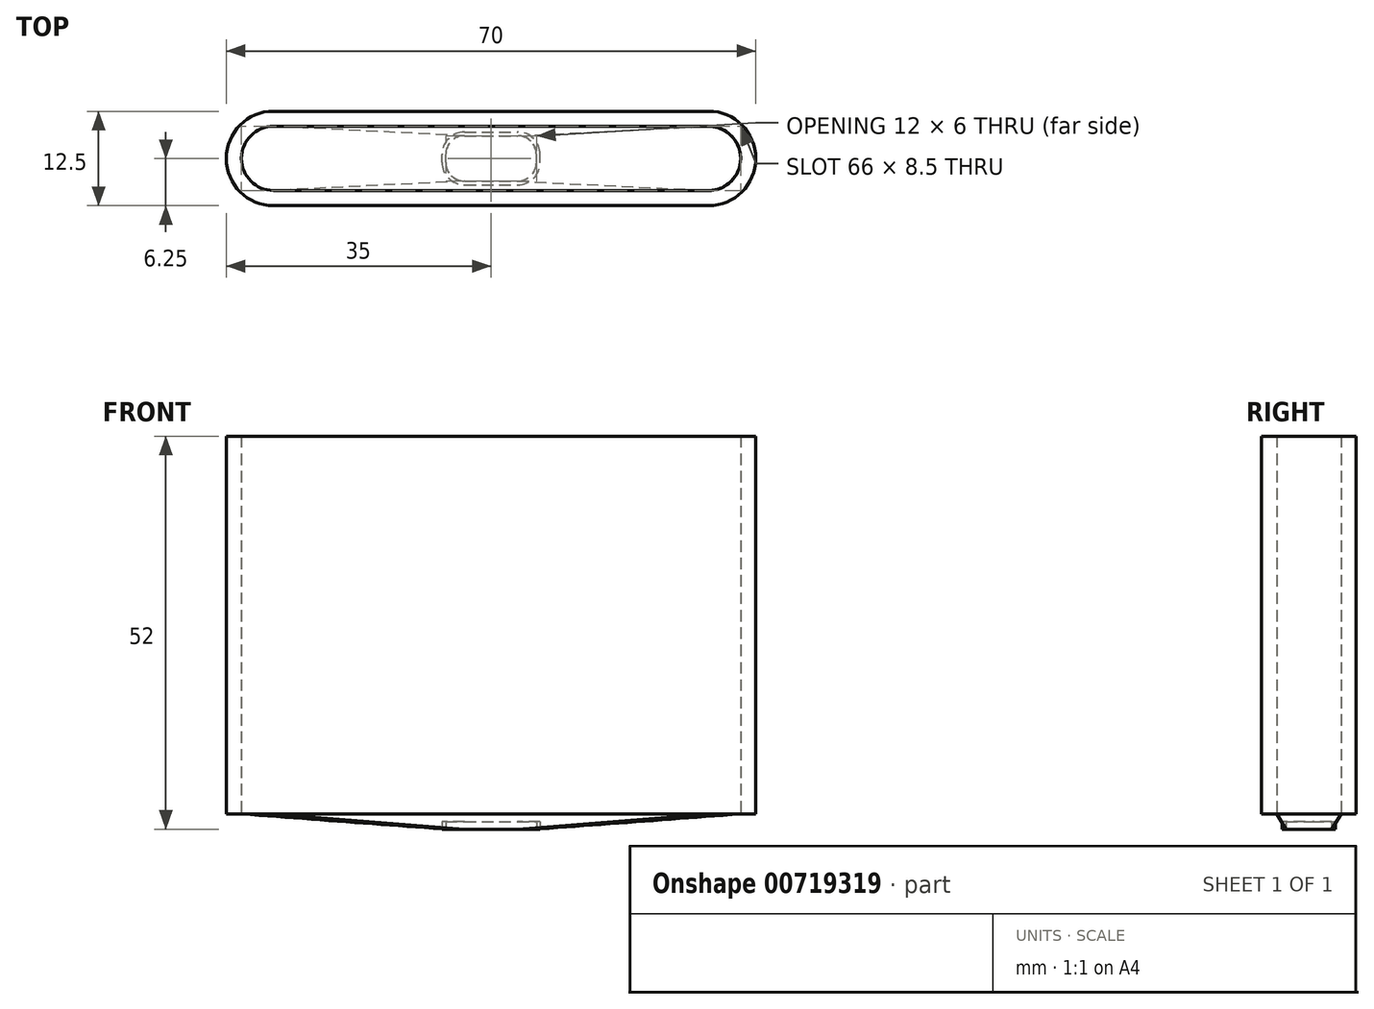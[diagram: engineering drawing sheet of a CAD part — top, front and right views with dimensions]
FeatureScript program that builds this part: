
annotation { "Feature Type Name" : "Feature", "Feature Type Description" : "" }
export const myFeature = defineFeature(function(context is Context, id is Id, definition is map)
    precondition{}
    {
        {
            var Q0;
            Q0=qCreatedBy(makeId("Top.planeOp"),FACE);
            var sketch = newSketch(context, id + "F0", { "sketchPlane" : qUnion([Q0])});
            skLineSegment(sketch, "E0.bottom", {"start": v(28.75, 6.25) * mm, "end": v(-28.75, 6.25) * mm});
            skLineSegment(sketch, "E0.top", {"start": v(28.75, -6.25) * mm, "end": v(-28.75, -6.25) * mm});
            skLineSegment(sketch, "E0.left", {"start": v(35, 0) * mm, "end": v(35, 0) * mm});
            skLineSegment(sketch, "E0.right", {"start": v(-35, 0) * mm, "end": v(-35, 0) * mm});
            skPoint(sketch, "E0.middle", {"position": v(0, 0) * mm});
            skLineSegment(sketch, "E1.bottom", {"start": v(-3.5, -3) * mm, "end": v(3.5, -3) * mm});
            skLineSegment(sketch, "E1.top", {"start": v(-3.5, 3) * mm, "end": v(3.5, 3) * mm});
            skLineSegment(sketch, "E1.left", {"start": v(-6, -0.5) * mm, "end": v(-6, 0.5) * mm});
            skLineSegment(sketch, "E1.right", {"start": v(6, -0.5) * mm, "end": v(6, 0.5) * mm});
            skLineSegment(sketch, "E2", {"start": v(0, -37.66) * mm, "end": v(0, 28.64) * mm, "construction": true});
            skLineSegment(sketch, "E3.bottom", {"start": v(13, 3) * mm, "end": v(26, 3) * mm});
            skLineSegment(sketch, "E3.top", {"start": v(13, -3) * mm, "end": v(26, -3) * mm});
            skLineSegment(sketch, "E3.left", {"start": v(10.5, 0.5) * mm, "end": v(10.5, -0.5) * mm});
            skLineSegment(sketch, "E3.right", {"start": v(28.5, 0.5) * mm, "end": v(28.5, -0.5) * mm});
            skPoint(sketch, "E4.visualSharp", {"position": v(-6, -3) * mm});
            skArc(sketch, "E4.filletArc", {"start": v(-6, -0.5) * mm, "mid": v(-5.27, -2.27) * mm, "end": v(-3.5, -3) * mm});
            skPoint(sketch, "E5.visualSharp", {"position": v(6, 3) * mm});
            skArc(sketch, "E5.filletArc", {"start": v(6, 0.5) * mm, "mid": v(5.27, 2.27) * mm, "end": v(3.5, 3) * mm});
            skPoint(sketch, "E6.visualSharp", {"position": v(6, -3) * mm});
            skArc(sketch, "E6.filletArc", {"start": v(3.5, -3) * mm, "mid": v(5.27, -2.27) * mm, "end": v(6, -0.5) * mm});
            skPoint(sketch, "E7.visualSharp", {"position": v(-6, 3) * mm});
            skArc(sketch, "E7.filletArc", {"start": v(-3.5, 3) * mm, "mid": v(-5.27, 2.27) * mm, "end": v(-6, 0.5) * mm});
            skLineSegment(sketch, "E8.MirrorCS", {"start": v(-13, 3) * mm, "end": v(-26, 3) * mm});
            skLineSegment(sketch, "E9.MirrorCS", {"start": v(-10.5, 0.5) * mm, "end": v(-10.5, -0.5) * mm});
            skLineSegment(sketch, "E10.MirrorCS", {"start": v(-13, -3) * mm, "end": v(-26, -3) * mm});
            skLineSegment(sketch, "E11.MirrorCS", {"start": v(-28.5, 0.5) * mm, "end": v(-28.5, -0.5) * mm});
            skPoint(sketch, "E12.visualSharp", {"position": v(10.5, -3) * mm});
            skArc(sketch, "E12.filletArc", {"start": v(10.5, -0.5) * mm, "mid": v(11.23, -2.27) * mm, "end": v(13, -3) * mm});
            skPoint(sketch, "E13.visualSharp", {"position": v(10.5, 3) * mm});
            skArc(sketch, "E13.filletArc", {"start": v(13, 3) * mm, "mid": v(11.23, 2.27) * mm, "end": v(10.5, 0.5) * mm});
            skPoint(sketch, "E14.visualSharp", {"position": v(28.5, 3) * mm});
            skArc(sketch, "E14.filletArc", {"start": v(28.5, 0.5) * mm, "mid": v(27.77, 2.27) * mm, "end": v(26, 3) * mm});
            skPoint(sketch, "E15.visualSharp", {"position": v(28.5, -3) * mm});
            skArc(sketch, "E15.filletArc", {"start": v(26, -3) * mm, "mid": v(27.77, -2.27) * mm, "end": v(28.5, -0.5) * mm});
            skPoint(sketch, "E16.visualSharp", {"position": v(-10.5, -3) * mm});
            skArc(sketch, "E16.filletArc", {"start": v(-13, -3) * mm, "mid": v(-11.23, -2.27) * mm, "end": v(-10.5, -0.5) * mm});
            skPoint(sketch, "E17.visualSharp", {"position": v(-10.5, 3) * mm});
            skArc(sketch, "E17.filletArc", {"start": v(-10.5, 0.5) * mm, "mid": v(-11.23, 2.27) * mm, "end": v(-13, 3) * mm});
            skPoint(sketch, "E18.visualSharp", {"position": v(-28.5, 3) * mm});
            skArc(sketch, "E18.filletArc", {"start": v(-26, 3) * mm, "mid": v(-27.77, 2.27) * mm, "end": v(-28.5, 0.5) * mm});
            skPoint(sketch, "E19.visualSharp", {"position": v(-28.5, -3) * mm});
            skArc(sketch, "E19.filletArc", {"start": v(-28.5, -0.5) * mm, "mid": v(-27.77, -2.27) * mm, "end": v(-26, -3) * mm});
            skPoint(sketch, "E20.visualSharp", {"position": v(-35, -6.25) * mm});
            skArc(sketch, "E20.filletArc", {"start": v(-35, 0) * mm, "mid": v(-33.17, -4.42) * mm, "end": v(-28.75, -6.25) * mm});
            skPoint(sketch, "E21.visualSharp", {"position": v(-35, 6.25) * mm});
            skArc(sketch, "E21.filletArc", {"start": v(-28.75, 6.25) * mm, "mid": v(-33.17, 4.42) * mm, "end": v(-35, 0) * mm});
            skPoint(sketch, "E22.visualSharp", {"position": v(35, 6.25) * mm});
            skArc(sketch, "E22.filletArc", {"start": v(35, 0) * mm, "mid": v(33.17, 4.42) * mm, "end": v(28.75, 6.25) * mm});
            skPoint(sketch, "E23.visualSharp", {"position": v(35, -6.25) * mm});
            skArc(sketch, "E23.filletArc", {"start": v(28.75, -6.25) * mm, "mid": v(33.17, -4.42) * mm, "end": v(35, 0) * mm});
            skArc(sketch, "E24.0", {"start": v(28.75, -4.25) * mm, "mid": v(31.76, -3) * mm, "end": v(33, 0) * mm});
            skArc(sketch, "E24.1", {"start": v(-33, 0) * mm, "mid": v(-31.76, -3) * mm, "end": v(-28.75, -4.25) * mm});
            skArc(sketch, "E24.2", {"start": v(-28.75, 4.25) * mm, "mid": v(-31.76, 3) * mm, "end": v(-33, 0) * mm});
            skLineSegment(sketch, "E24.3", {"start": v(28.75, -4.25) * mm, "end": v(-28.75, -4.25) * mm});
            skLineSegment(sketch, "E24.4", {"start": v(28.75, 4.25) * mm, "end": v(-28.75, 4.25) * mm});
            skArc(sketch, "E24.5", {"start": v(33, 0) * mm, "mid": v(31.76, 3) * mm, "end": v(28.75, 4.25) * mm});
            skLineSegment(sketch, "E25", {"start": v(-28.75, -4.25) * mm, "end": v(-28.75, -6.25) * mm});
            skLineSegment(sketch, "E26", {"start": v(28.75, -6.25) * mm, "end": v(28.75, -4.25) * mm});
            skPoint(sketch, "E27.startSnap0", {"position": v(19.5, 0) * mm});
            skLineSegment(sketch, "E28.0", {"start": v(-3.5, 3.5) * mm, "end": v(3.5, 3.5) * mm});
            skArc(sketch, "E28.1", {"start": v(6.5, 0.5) * mm, "mid": v(5.62, 2.62) * mm, "end": v(3.5, 3.5) * mm});
            skArc(sketch, "E28.2", {"start": v(-3.5, 3.5) * mm, "mid": v(-5.62, 2.62) * mm, "end": v(-6.5, 0.5) * mm});
            skLineSegment(sketch, "E28.3", {"start": v(6.5, -0.5) * mm, "end": v(6.5, 0.5) * mm});
            skLineSegment(sketch, "E28.4", {"start": v(-6.5, -0.5) * mm, "end": v(-6.5, 0.5) * mm});
            skArc(sketch, "E28.5", {"start": v(-6.5, -0.5) * mm, "mid": v(-5.62, -2.62) * mm, "end": v(-3.5, -3.5) * mm});
            skLineSegment(sketch, "E28.6", {"start": v(-3.5, -3.5) * mm, "end": v(3.5, -3.5) * mm});
            skArc(sketch, "E28.7", {"start": v(3.5, -3.5) * mm, "mid": v(5.62, -2.62) * mm, "end": v(6.5, -0.5) * mm});
            skSolve(sketch);
        }
        {
            var Q0;
            Q0=sQuery(id+"F0.wireOp",EDGE,"E0.top");
            cPlane(context, id + "F1", {"entities" : qUnion([Q0]), "cplaneType" : CPlaneType.LINE_ANGLE, "offset" : 25 * mm, "angle" : 0 * degree, "width" : 150 * mm, "height" : 150 * mm});
        }
        {
            var Q0;
            Q0=qCreatedBy(id+"F1.planeOp",FACE);
            var sketch = newSketch(context, id + "F2", { "sketchPlane" : qUnion([Q0])});
            skLineSegment(sketch, "E29.bottom", {"start": v(-28.75, 0) * mm, "end": v(28.75, 0) * mm});
            skLineSegment(sketch, "E29.top", {"start": v(-28.75, 17) * mm, "end": v(-11, 17) * mm});
            skLineSegment(sketch, "E29.left", {"start": v(-28.75, 0) * mm, "end": v(-28.75, 17) * mm});
            skLineSegment(sketch, "E29.right", {"start": v(28.75, 0) * mm, "end": v(28.75, 17) * mm});
            skLineSegment(sketch, "E30.trimOffspring", {"start": v(11, 17) * mm, "end": v(28.75, 17) * mm});
            skLineSegment(sketch, "E31.top", {"start": v(0, 6) * mm, "end": v(0, 6) * mm});
            skLineSegment(sketch, "E31.left", {"start": v(-6, 12) * mm, "end": v(-6, 12) * mm});
            skLineSegment(sketch, "E31.right", {"start": v(6, 12) * mm, "end": v(6, 12) * mm});
            skPoint(sketch, "E31.middle", {"position": v(0, 14.54) * mm});
            skPoint(sketch, "E32.orphan", {"position": v(6, 23.08) * mm});
            skPoint(sketch, "E33.orphan", {"position": v(-6, 23.08) * mm});
            skPoint(sketch, "E34.visualSharp", {"position": v(-6, 6) * mm});
            skArc(sketch, "E34.filletArc", {"start": v(-6, 12) * mm, "mid": v(-4.24, 7.76) * mm, "end": v(0, 6) * mm});
            skPoint(sketch, "E35.visualSharp", {"position": v(6, 6) * mm});
            skArc(sketch, "E35.filletArc", {"start": v(0, 6) * mm, "mid": v(4.24, 7.76) * mm, "end": v(6, 12) * mm});
            skPoint(sketch, "E36.visualSharp", {"position": v(6, 17) * mm});
            skArc(sketch, "E36.filletArc", {"start": v(11, 17) * mm, "mid": v(7.46, 15.54) * mm, "end": v(6, 12) * mm});
            skPoint(sketch, "E37.visualSharp", {"position": v(-6, 17) * mm});
            skArc(sketch, "E37.filletArc", {"start": v(-6, 12) * mm, "mid": v(-7.46, 15.54) * mm, "end": v(-11, 17) * mm});
            skSolve(sketch);
        }
        {
            var Q0;
            Q0=qCreatedBy(makeId("Top.planeOp"),FACE);
            cPlane(context, id + "F3", {"entities" : qUnion([Q0]), "cplaneType" : CPlaneType.OFFSET, "offset" : 2 * mm, "width" : 150 * mm, "height" : 150 * mm});
        }
        {
            var Q0;
            Q0=qCreatedBy(id+"F3.planeOp",FACE);
            var sketch = newSketch(context, id + "F4", { "sketchPlane" : qUnion([Q0])});
            skArc(sketch, "E38.0", {"start": v(-33, 0) * mm, "mid": v(-32.94, -0.73) * mm, "end": v(-32.75, -1.44) * mm});
            skArc(sketch, "E38.1", {"start": v(-28.75, 4.25) * mm, "mid": v(-31.1, 3.54) * mm, "end": v(-32.66, 1.66) * mm});
            skLineSegment(sketch, "E38.2", {"start": v(28.75, 4.25) * mm, "end": v(-28.75, 4.25) * mm});
            skArc(sketch, "E38.3", {"start": v(33, 0) * mm, "mid": v(32.92, 0.8) * mm, "end": v(32.7, 1.57) * mm});
            skArc(sketch, "E38.4", {"start": v(28.75, -4.25) * mm, "mid": v(31.08, -3.55) * mm, "end": v(32.65, -1.7) * mm});
            skArc(sketch, "E38.5", {"start": v(28.75, -6.25) * mm, "mid": v(33.17, -4.42) * mm, "end": v(35, 0) * mm});
            skArc(sketch, "E38.6", {"start": v(35, 0) * mm, "mid": v(33.17, 4.42) * mm, "end": v(28.75, 6.25) * mm});
            skLineSegment(sketch, "E38.7", {"start": v(28.75, 6.25) * mm, "end": v(-28.75, 6.25) * mm});
            skArc(sketch, "E38.8", {"start": v(-28.75, 6.25) * mm, "mid": v(-33.17, 4.42) * mm, "end": v(-35, 0) * mm});
            skArc(sketch, "E38.9", {"start": v(-35, 0) * mm, "mid": v(-33.17, -4.42) * mm, "end": v(-28.75, -6.25) * mm});
            skLineSegment(sketch, "E39", {"start": v(-28.75, -4.25) * mm, "end": v(28.75, -4.25) * mm});
            skLineSegment(sketch, "E40", {"start": v(-28.75, -6.25) * mm, "end": v(28.75, -6.25) * mm});
            skPoint(sketch, "E38.10.end.orphan", {"position": v(-28.75, -6.25) * mm});
            skPoint(sketch, "E38.10.start.orphan", {"position": v(-28.75, -4.25) * mm});
            skPoint(sketch, "E38.11.end.orphan", {"position": v(28.75, -4.25) * mm});
            skPoint(sketch, "E38.11.start.orphan", {"position": v(28.75, -6.25) * mm});
            skArc(sketch, "E41", {"start": v(-32.75, -1.44) * mm, "mid": v(-31.2, -3.48) * mm, "end": v(-28.75, -4.25) * mm});
            skArc(sketch, "E42", {"start": v(-32.66, 1.66) * mm, "mid": v(-32.91, 0.85) * mm, "end": v(-33, 0) * mm});
            skArc(sketch, "E43", {"start": v(32.7, 1.57) * mm, "mid": v(31.13, 3.52) * mm, "end": v(28.75, 4.25) * mm});
            skArc(sketch, "E44", {"start": v(32.65, -1.7) * mm, "mid": v(32.91, -0.86) * mm, "end": v(33, 0) * mm});
            skSolve(sketch);
        }
        {
            var Q0;
            Q0=qCreatedBy(makeId("Top.planeOp"),FACE);
            cPlane(context, id + "F5", {"entities" : qUnion([Q0]), "cplaneType" : CPlaneType.OFFSET, "offset" : 0 * mm, "width" : 150 * mm, "height" : 150 * mm});
        }
        {
            var Q0;
            Q0=qCreatedBy(id+"F5.planeOp",FACE);
            var sketch = newSketch(context, id + "F6", { "sketchPlane" : qUnion([Q0])});
            skArc(sketch, "E45.0", {"start": v(-6.5, -0.5) * mm, "mid": v(-5.62, -2.62) * mm, "end": v(-3.5, -3.5) * mm});
            skLineSegment(sketch, "E45.1", {"start": v(6.5, -0.5) * mm, "end": v(6.5, 0.5) * mm});
            skArc(sketch, "E45.2", {"start": v(6.5, 0.5) * mm, "mid": v(5.62, 2.62) * mm, "end": v(3.5, 3.5) * mm});
            skLineSegment(sketch, "E45.3", {"start": v(-3.5, 3.5) * mm, "end": v(3.5, 3.5) * mm});
            skArc(sketch, "E45.4", {"start": v(-3.5, 3.5) * mm, "mid": v(-5.62, 2.62) * mm, "end": v(-6.5, 0.5) * mm});
            skLineSegment(sketch, "E45.5", {"start": v(-6.5, -0.5) * mm, "end": v(-6.5, 0.5) * mm});
            skLineSegment(sketch, "E45.6", {"start": v(-3.5, -3.5) * mm, "end": v(3.5, -3.5) * mm});
            skArc(sketch, "E45.7", {"start": v(3.5, -3.5) * mm, "mid": v(5.62, -2.62) * mm, "end": v(6.5, -0.5) * mm});
            skArc(sketch, "E45.8", {"start": v(3.5, -3) * mm, "mid": v(5.27, -2.27) * mm, "end": v(6, -0.5) * mm});
            skLineSegment(sketch, "E45.9", {"start": v(6, -0.5) * mm, "end": v(6, 0.5) * mm});
            skArc(sketch, "E45.10", {"start": v(6, 0.5) * mm, "mid": v(5.27, 2.27) * mm, "end": v(3.5, 3) * mm});
            skLineSegment(sketch, "E45.11", {"start": v(-3.5, 3) * mm, "end": v(3.5, 3) * mm});
            skArc(sketch, "E45.12", {"start": v(-3.5, 3) * mm, "mid": v(-5.27, 2.27) * mm, "end": v(-6, 0.5) * mm});
            skLineSegment(sketch, "E45.13", {"start": v(-6, -0.5) * mm, "end": v(-6, 0.5) * mm});
            skArc(sketch, "E45.14", {"start": v(-6, -0.5) * mm, "mid": v(-5.27, -2.27) * mm, "end": v(-3.5, -3) * mm});
            skLineSegment(sketch, "E45.15", {"start": v(-3.5, -3) * mm, "end": v(3.5, -3) * mm});
            skSolve(sketch);
        }
        {
            var Q0;
            Q0 = qSketchRegion(id + "F6", true);
            extrude(context, id + "F7", {"entities" : qUnion([Q0]), "depth" : 1 * mm, "offsetDistance" : 25 * mm});
        }
        {
            var Q0;
            Q0 = qSketchRegion(id + "F4", true);
            extrude(context, id + "F8", {"entities" : qUnion([Q0]), "depth" : 50 * mm, "offsetDistance" : 25 * mm});
        }
        {
            var Q0;
            Q0=makeQuery(id+"F0.imprint","IMPRINT",FACE,{"disambiguationData":[TD([[makeQuery(id+"F0.imprint","IMPRINT",EDGE,{"derivedFrom":sQuery(id+"F0.wireOp",EDGE,"E1.bottom")}),1.0]])]});
            var Q1;
            Q1=makeQuery(id+"F4.imprint","IMPRINT",FACE,{"disambiguationData":[TD([[makeQuery(id+"F4.imprint","IMPRINT",EDGE,{"derivedFrom":sQuery(id+"F4.wireOp",EDGE,"E38.0")}),1.0]])]});
            var Q2;
            Q2 = qConstructionFilter(qBodyType(qCreatedBy(id + "F10" ,EDGE), BodyType.WIRE), ConstructionObject.NO);
            loft(context, id + "F9", {"addGuides" : true, "sheetProfilesArray" : [{ "sheetProfileEntities" : qUnion([Q0]) }, { "sheetProfileEntities" : qUnion([Q1]) }], "guidesArray" : [{ "guideEntities" : qUnion([Q2]), "guideDerivativeType" : LoftGuideDerivativeType.DEFAULT, "guideDerivativeMagnitude" : 1 }]});
        }
    });
